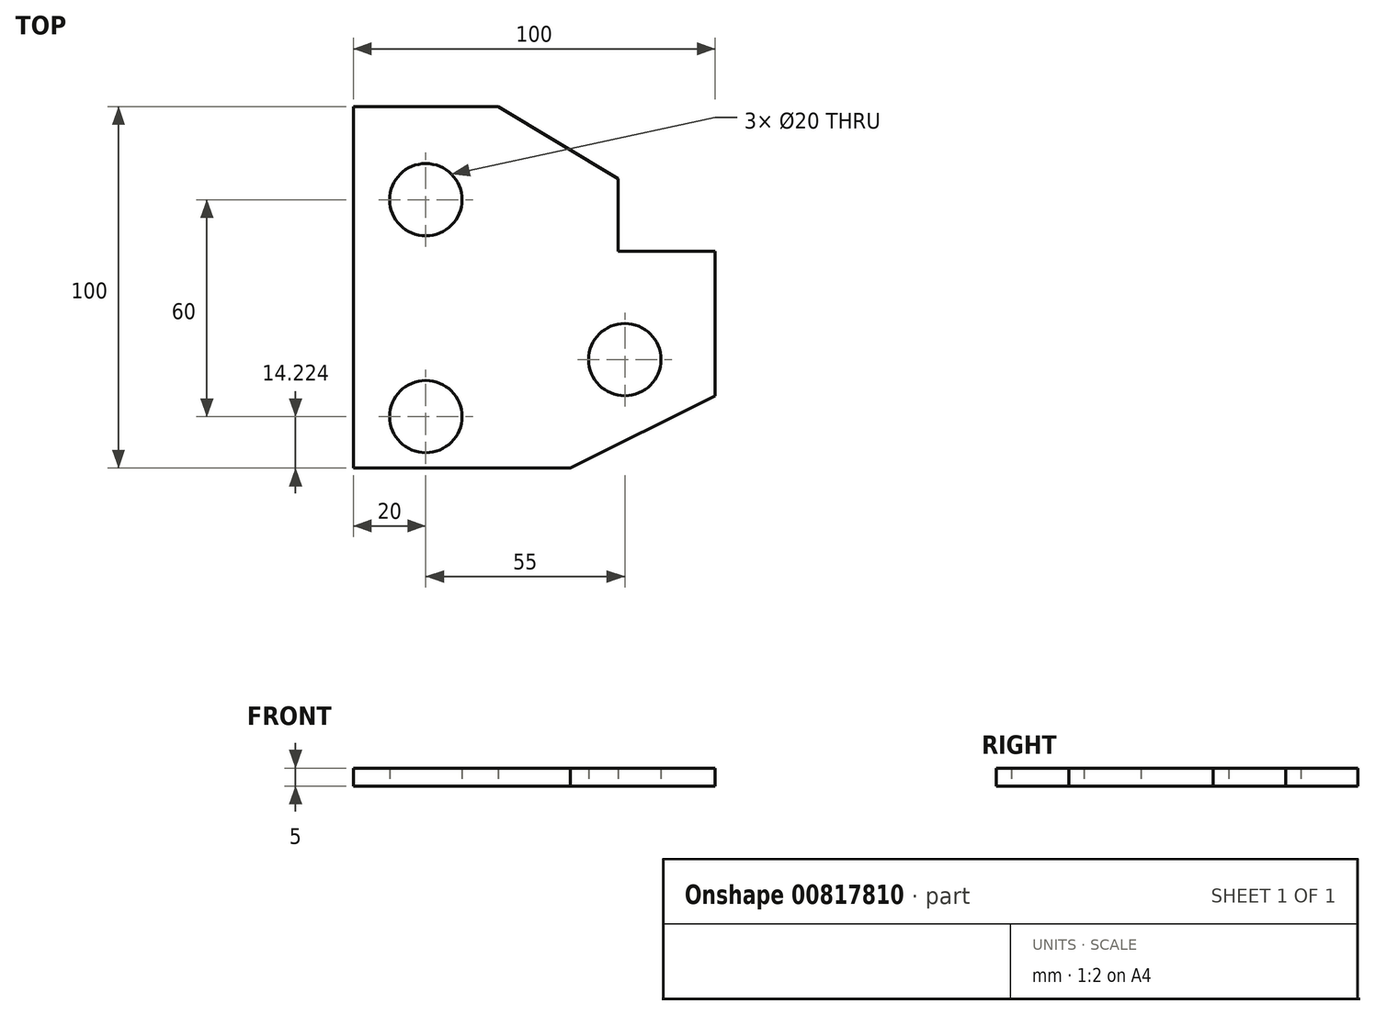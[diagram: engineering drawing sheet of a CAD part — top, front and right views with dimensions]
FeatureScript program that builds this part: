
annotation { "Feature Type Name" : "Feature", "Feature Type Description" : "" }
export const myFeature = defineFeature(function(context is Context, id is Id, definition is map)
    precondition{}
    {
        {
            var Q0;
            Q0=qCreatedBy(makeId("Top.planeOp"),FACE);
            var sketch = newSketch(context, id + "F0", { "sketchPlane" : qUnion([Q0])});
            skLineSegment(sketch, "E0", {"start": v(0, 0) * mm, "end": v(60, 0) * mm});
            skLineSegment(sketch, "E1", {"start": v(60, 0) * mm, "end": v(100, 20) * mm});
            skLineSegment(sketch, "E2", {"start": v(100, 20) * mm, "end": v(100, 60) * mm});
            skLineSegment(sketch, "E3", {"start": v(100, 60) * mm, "end": v(73.18, 60) * mm});
            skLineSegment(sketch, "E4", {"start": v(73.18, 60) * mm, "end": v(73.18, 80) * mm});
            skLineSegment(sketch, "E5", {"start": v(73.18, 80) * mm, "end": v(40, 100) * mm});
            skLineSegment(sketch, "E6", {"start": v(40, 100) * mm, "end": v(0, 100) * mm});
            skLineSegment(sketch, "E7", {"start": v(0, 100) * mm, "end": v(0, 0) * mm});
            skCircle(sketch, "E8", {"center": v(20, 14.22) * mm, "radius": 10 * mm});
            skCircle(sketch, "E9", {"center": v(20, 74.22) * mm, "radius": 10 * mm});
            skCircle(sketch, "E10", {"center": v(75, 30) * mm, "radius": 10 * mm});
            skSolve(sketch);
        }
        {
            var Q0;
            Q0=makeQuery(id+"F0.imprint","IMPRINT",FACE,{"disambiguationData":[TD([[makeQuery(id+"F0.imprint","IMPRINT",EDGE,{"derivedFrom":sQuery(id+"F0.wireOp",EDGE,"E0")}),1.0]])]});
            extrude(context, id + "F1", {"entities" : qUnion([Q0]), "depth" : 5 * mm, "offsetDistance" : 25 * mm});
        }
    });
